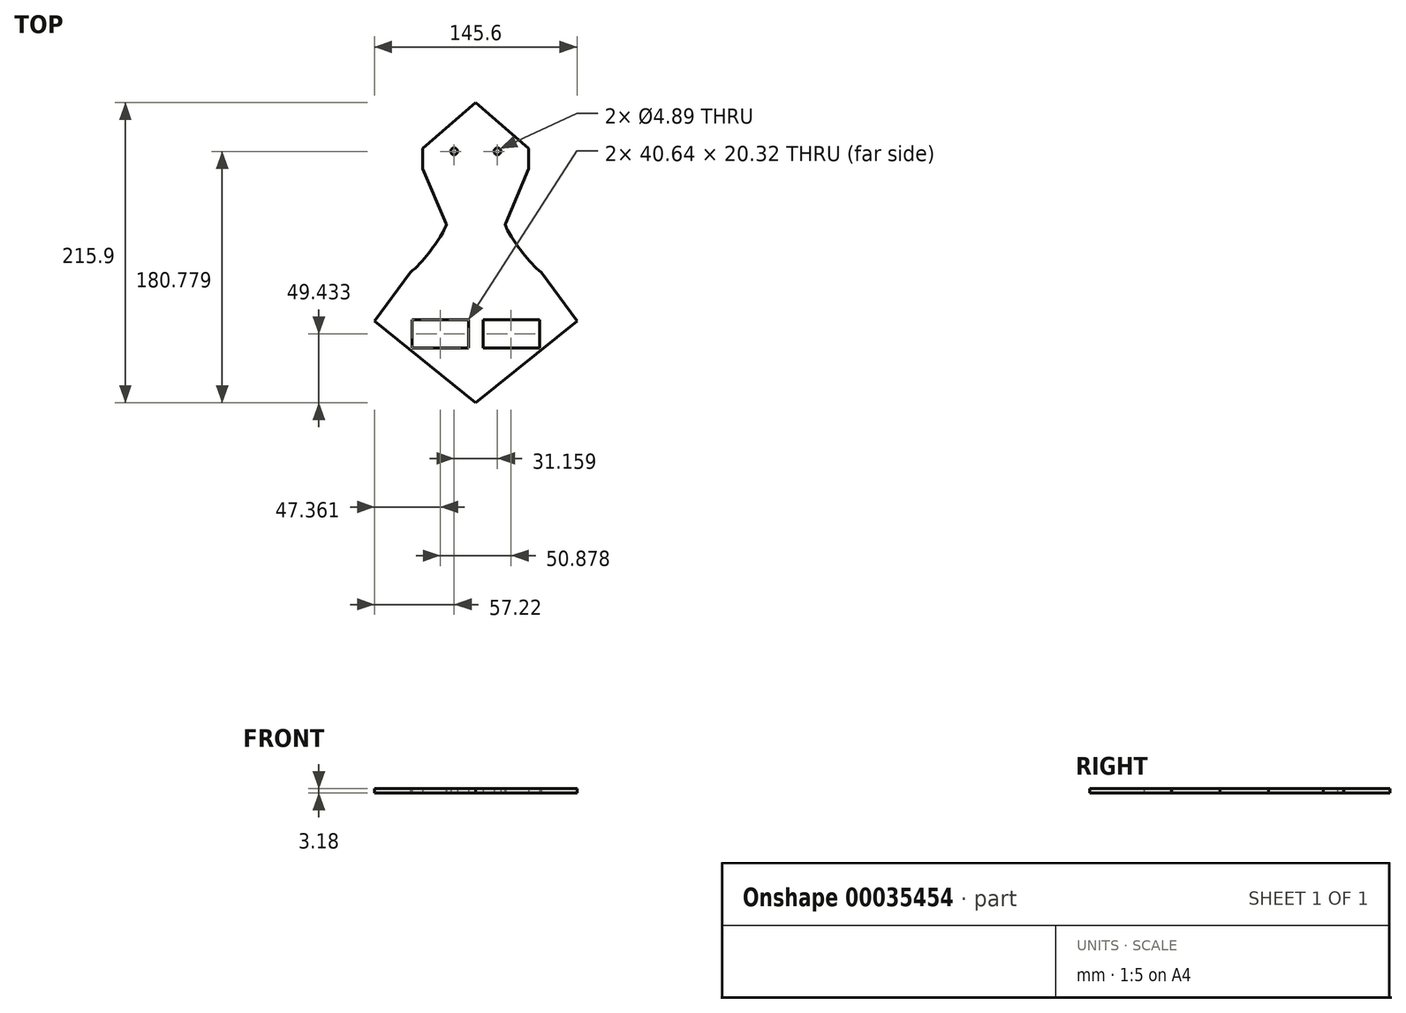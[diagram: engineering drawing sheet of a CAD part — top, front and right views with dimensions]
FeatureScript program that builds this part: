
annotation { "Feature Type Name" : "Feature", "Feature Type Description" : "" }
export const myFeature = defineFeature(function(context is Context, id is Id, definition is map)
    precondition{}
    {
        {
            var Q0;
            Q0=qCreatedBy(makeId("Top.planeOp"),FACE);
            var sketch = newSketch(context, id + "F0", { "sketchPlane" : qUnion([Q0])});
            skLineSegment(sketch, "E0", {"start": v(0, 113.75) * mm, "end": v(0, -102.15) * mm, "construction": true});
            skLineSegment(sketch, "E1.MirrorCS", {"start": v(-72.8, -43.4) * mm, "end": v(-47.07, -8.4) * mm});
            skLineSegment(sketch, "E2.MirrorCS", {"start": v(72.8, -43.4) * mm, "end": v(47.07, -8.4) * mm});
            skLineSegment(sketch, "E3.MirrorCS", {"start": v(38.11, 80.63) * mm, "end": v(0, 113.75) * mm});
            skFitSpline(sketch, "E4", {"points": [v(47.07, -8.4) * mm, v(81.79, 0) * mm, v(127.95, 56.34) * mm, v(107.96, 41.44) * mm, v(111.96, 65.43) * mm, v(94.88, 38.9) * mm, v(90.51, 66.89) * mm, v(82.88, 38.9) * mm, v(57.07, 0) * mm, v(21.33, 26.58) * mm, v(47.07, -8.4) * mm]});
            skFitSpline(sketch, "E5.MirrorCS", {"points": [v(-47.07, -8.4) * mm, v(-81.79, 0) * mm, v(-127.95, 56.34) * mm, v(-107.96, 41.44) * mm, v(-111.96, 65.43) * mm, v(-94.88, 38.9) * mm, v(-90.51, 66.89) * mm, v(-82.88, 38.9) * mm, v(-57.07, 0) * mm, v(-21.33, 26.58) * mm, v(-47.07, -8.4) * mm]});
            skLineSegment(sketch, "E6", {"start": v(38.11, 80.63) * mm, "end": v(38.11, 66.01) * mm});
            skLineSegment(sketch, "E7", {"start": v(38.11, 66.01) * mm, "end": v(21.33, 26.58) * mm});
            skLineSegment(sketch, "E8.trimOffspring", {"start": v(7.72, -93.78) * mm, "end": v(8.34, -94.45) * mm});
            skLineSegment(sketch, "E9", {"start": v(72.8, -43.4) * mm, "end": v(0, -102.15) * mm});
            skLineSegment(sketch, "E10", {"start": v(-72.8, -43.4) * mm, "end": v(0, -102.15) * mm});
            skLineSegment(sketch, "E11.MirrorCS", {"start": v(-38.11, 80.63) * mm, "end": v(0, 113.75) * mm});
            skLineSegment(sketch, "E12.MirrorCS", {"start": v(-38.11, 80.63) * mm, "end": v(-38.11, 66.01) * mm});
            skLineSegment(sketch, "E13.MirrorCS", {"start": v(-38.11, 66.01) * mm, "end": v(-21.33, 26.58) * mm});
            skLineSegment(sketch, "E14.rect.bottom", {"start": v(-5.12, -42.56) * mm, "end": v(-45.76, -42.56) * mm});
            skLineSegment(sketch, "E14.rect.top", {"start": v(-5.12, -62.88) * mm, "end": v(-45.76, -62.88) * mm});
            skLineSegment(sketch, "E14.rect.left", {"start": v(-5.12, -42.56) * mm, "end": v(-5.12, -62.88) * mm});
            skLineSegment(sketch, "E14.rect.right", {"start": v(-45.76, -42.56) * mm, "end": v(-45.76, -62.88) * mm});
            skPoint(sketch, "E14.rect.middle", {"position": v(-25.44, -52.72) * mm});
            skLineSegment(sketch, "E15.MirrorCS", {"start": v(5.12, -62.88) * mm, "end": v(45.76, -62.88) * mm});
            skLineSegment(sketch, "E16.MirrorCS", {"start": v(5.12, -42.56) * mm, "end": v(5.12, -62.88) * mm});
            skLineSegment(sketch, "E17.MirrorCS", {"start": v(45.76, -42.56) * mm, "end": v(45.76, -62.88) * mm});
            skLineSegment(sketch, "E18.MirrorCS", {"start": v(5.12, -42.56) * mm, "end": v(45.76, -42.56) * mm});
            skCircle(sketch, "E19", {"center": v(-15.58, 78.63) * mm, "radius": 2.44 * mm});
            skCircle(sketch, "E20.MirrorC", {"center": v(15.58, 78.63) * mm, "radius": 2.44 * mm});
            skSolve(sketch);
        }
        {
            var Q0;
            Q0=makeQuery(id+"F0.imprint","IMPRINT",FACE,{"disambiguationData":[TD([[makeQuery(id+"F0.imprint","IMPRINT",EDGE,{"derivedFrom":sQuery(id+"F0.wireOp",EDGE,"E1.MirrorCS")}),-1.0]])]});
            extrude(context, id + "F1", {"entities" : qUnion([Q0]), "depth" : 3.17 * mm});
        }
        {
            var Q0;
            Q0=makeQuery(id+"F0.imprint","IMPRINT",FACE,{"disambiguationData":[TD([[makeQuery(id+"F0.imprint","IMPRINT",EDGE,{"derivedFrom":sQuery(id+"F0.wireOp",EDGE,"E14.rect.bottom")}),1.0]])]});
            extrude(context, id + "F2", {"entities" : qUnion([Q0]), "operationType" : NewBodyOperationType.REMOVE, "oppositeDirection" : true, "depth" : 25.4 * mm});
        }
        {
            var Q0;
            Q0=makeQuery(id+"F0.imprint","IMPRINT",FACE,{"disambiguationData":[TD([[makeQuery(id+"F0.imprint","IMPRINT",EDGE,{"derivedFrom":sQuery(id+"F0.wireOp",EDGE,"E16.MirrorCS")}),1.0]])]});
            extrude(context, id + "F3", {"entities" : qUnion([Q0]), "operationType" : NewBodyOperationType.REMOVE, "oppositeDirection" : true, "depth" : 25.4 * mm});
        }
    });
